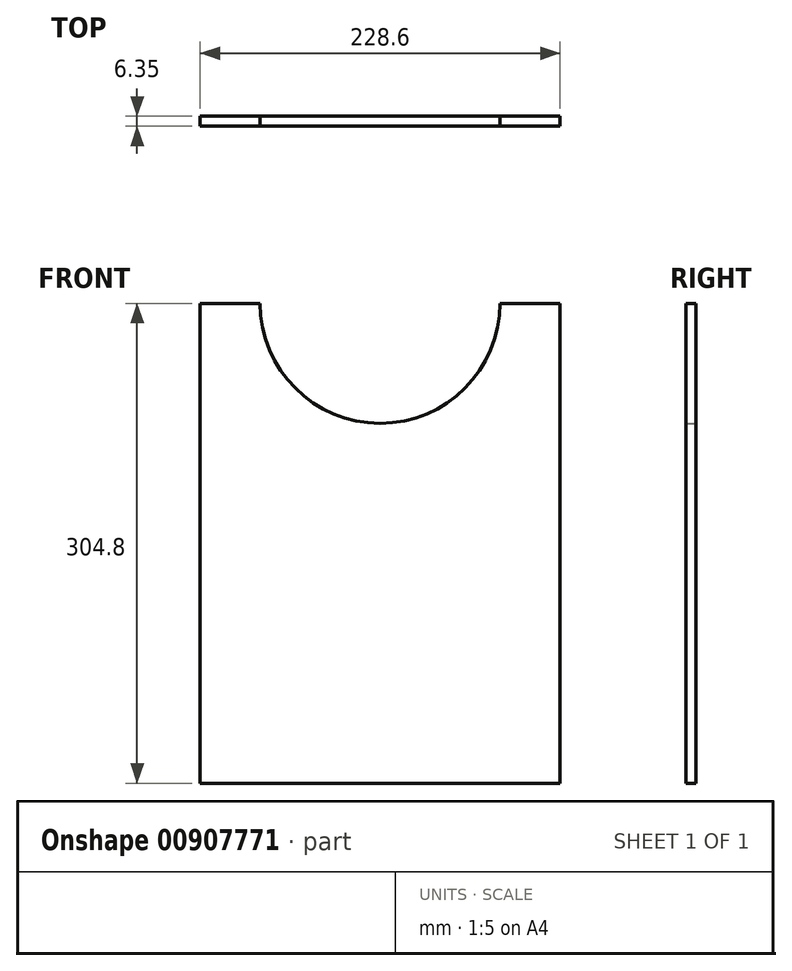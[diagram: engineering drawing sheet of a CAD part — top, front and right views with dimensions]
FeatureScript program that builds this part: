
annotation { "Feature Type Name" : "Feature", "Feature Type Description" : "" }
export const myFeature = defineFeature(function(context is Context, id is Id, definition is map)
    precondition{}
    {
        {
            var Q0;
            Q0=qCreatedBy(makeId("Front.planeOp"),FACE);
            var sketch = newSketch(context, id + "F0", { "sketchPlane" : qUnion([Q0])});
            skLineSegment(sketch, "E0.bottom", {"start": v(114.3, -152.4) * mm, "end": v(-114.3, -152.4) * mm});
            skLineSegment(sketch, "E0.top", {"start": v(114.3, 152.4) * mm, "end": v(76.2, 152.4) * mm});
            skLineSegment(sketch, "E0.left", {"start": v(114.3, -152.4) * mm, "end": v(114.3, 152.4) * mm});
            skLineSegment(sketch, "E0.right", {"start": v(-114.3, -152.4) * mm, "end": v(-114.3, 152.4) * mm});
            skPoint(sketch, "E0.middle", {"position": v(0, 0) * mm});
            skArc(sketch, "E1", {"start": v(-76.2, 152.4) * mm, "mid": v(0, 76.2) * mm, "end": v(76.2, 152.4) * mm});
            skLineSegment(sketch, "E2.trimOffspring", {"start": v(-76.2, 152.4) * mm, "end": v(-114.3, 152.4) * mm});
            skSolve(sketch);
        }
        {
            var Q0;
            Q0=makeQuery(id+"F0.imprint","IMPRINT",FACE,{"disambiguationData":[TD([[makeQuery(id+"F0.imprint","IMPRINT",EDGE,{"derivedFrom":sQuery(id+"F0.wireOp",EDGE,"E0.bottom")}),-1.0]])]});
            extrude(context, id + "F1", {"entities" : qUnion([Q0]), "depth" : 6.35 * mm, "offsetDistance" : 25.4 * mm});
        }
    });
